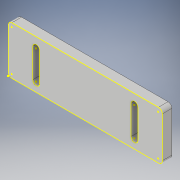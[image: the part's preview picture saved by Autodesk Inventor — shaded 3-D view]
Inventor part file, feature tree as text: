
AUTODESK INVENTOR PART (.ipt)
format: ipt  version: 2019 (Build 230136000, 136)  size: 138,240 bytes
history: native  units: mm
features: sketch x4, extrude x2, hole x1, fillet x1, projected_geometry x1
ambient origin geometry x8: Origin, YZ Plane, XZ Plane, XY Plane, X Axis, Y Axis, Z Axis, Center Point
bodies: Solid1 (feature_tree)
feature tree (9):
  sketch  "Sketch1"  dims[d0=80.0mm d1=25.0mm]
  extrude  "Extrusion1"  Depth=25.0mm
  hole  "Hole1"  [1 undecoded]
  extrude  "Extrusion2"  Depth=5.0mm TaperAngle=0.0deg
  fillet  "Fillet1"  Radius=5.0mm
  sketch  "Sketch4"  dims[d5=80.0mm d6=25.0mm d7=14.5mm d8=51.0mm d9=15.0mm d10=5.0mm d11=0.0mm d12=3.5mm d13=6.0mm d14=4.0mm d15=2.0mm d16=90.0deg d17=8.0mm d18=20.594885mm d19=5.0mm d20=0.0mm d21=2.0mm]
  sketch  "Sketch2"  dims[d2=14.5mm d3=51.0mm]
  sketch  "Sketch3"  dims[d4=15.0mm]
  projected_geometry  "Projected Loop1"
note: 1 required parameter value undecoded (feature->parameter linkage not recoverable at this tier; creation-order binding heuristic only, values carry confidence <= 0.55)
